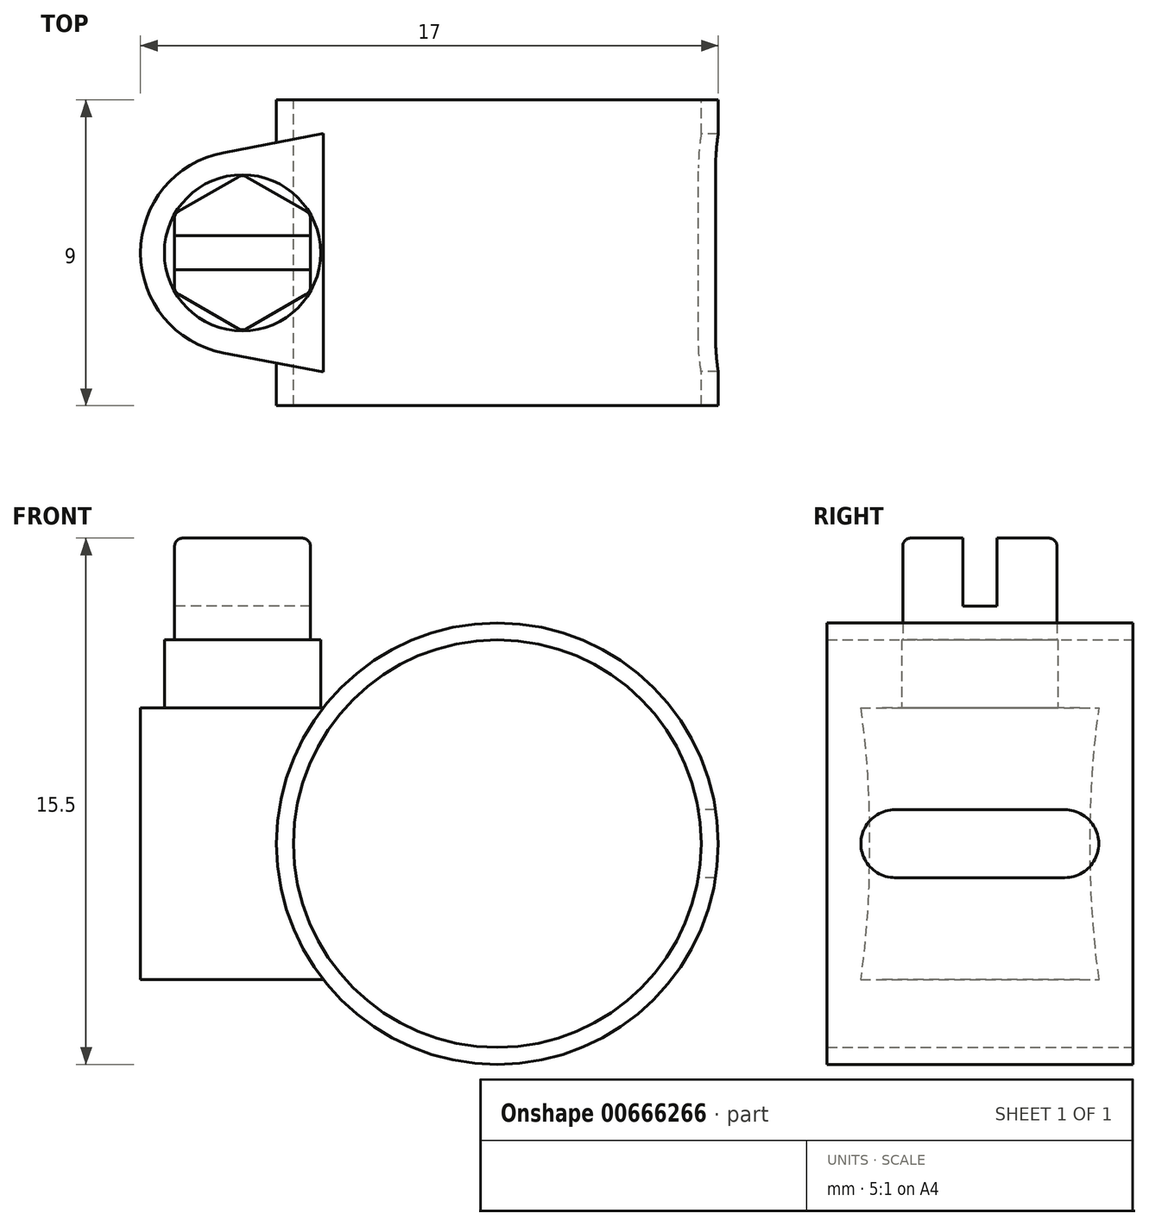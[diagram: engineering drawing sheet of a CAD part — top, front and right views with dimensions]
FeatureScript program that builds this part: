
annotation { "Feature Type Name" : "Feature", "Feature Type Description" : "" }
export const myFeature = defineFeature(function(context is Context, id is Id, definition is map)
    precondition{}
    {
        {
            var Q0;
            Q0=qCreatedBy(makeId("Front.planeOp"),FACE);
            var sketch = newSketch(context, id + "F0", { "sketchPlane" : qUnion([Q0])});
            skCircle(sketch, "E0", {"center": v(0, 0) * mm, "radius": 6.5 * mm});
            skCircle(sketch, "E1", {"center": v(0, 0) * mm, "radius": 6 * mm, "construction": true});
            skSolve(sketch);
        }
        {
            var Q0;
            Q0=qSketchRegion(id+"F0",true);
            extrude(context, id + "F1", {"entities" : qUnion([Q0]), "depth" : 9 * mm, "offsetDistance" : 25 * mm, "symmetric" : true});
        }
        {
            var Q0;
            Q0=qCreatedBy(makeId("Top.planeOp"),FACE);
            var sketch = newSketch(context, id + "F2", { "sketchPlane" : qUnion([Q0])});
            skArc(sketch, "E2", {"start": v(-8.07, 2.95) * mm, "mid": v(-10.5, 0) * mm, "end": v(-8.07, -2.95) * mm});
            skLineSegment(sketch, "E3", {"start": v(-8.07, 2.95) * mm, "end": v(0, 4.5) * mm});
            skLineSegment(sketch, "E4", {"start": v(0, 4.5) * mm, "end": v(0, -4.5) * mm});
            skLineSegment(sketch, "E5", {"start": v(0, -4.5) * mm, "end": v(-8.07, -2.95) * mm});
            skSolve(sketch);
        }
        {
            var Q0;
            Q0=qSketchRegion(id+"F2",true);
            extrude(context, id + "F3", {"entities" : qUnion([Q0]), "operationType" : NewBodyOperationType.ADD, "depth" : 8 * mm, "offsetDistance" : 25 * mm, "symmetric" : true});
        }
        {
            var Q0;
            Q0=makeQuery(id+"F3.opExtrude","CAP_FACE",FACE,{"disambiguationData":[OSD([sQuery(id+"F2.wireOp",EDGE,"E2"),sQuery(id+"F2.wireOp",EDGE,"E3"),sQuery(id+"F2.wireOp",EDGE,"E4"),sQuery(id+"F2.wireOp",EDGE,"E5")])],"isStart":false});
            var sketch = newSketch(context, id + "F4", { "sketchPlane" : qUnion([Q0])});
            skCircle(sketch, "E6.cCircle", {"center": v(-7.5, 0) * mm, "radius": 2 * mm, "construction": true});
            skLineSegment(sketch, "E6.0", {"start": v(-9.5, -1.15) * mm, "end": v(-9.5, 1.15) * mm});
            skLineSegment(sketch, "E6.1", {"start": v(-9.5, 1.15) * mm, "end": v(-7.5, 2.3) * mm});
            skLineSegment(sketch, "E6.2", {"start": v(-7.5, 2.3) * mm, "end": v(-5.5, 1.15) * mm});
            skLineSegment(sketch, "E6.3", {"start": v(-5.5, 1.15) * mm, "end": v(-5.5, -1.15) * mm});
            skLineSegment(sketch, "E6.4", {"start": v(-5.5, -1.15) * mm, "end": v(-7.5, -2.3) * mm});
            skLineSegment(sketch, "E6.5", {"start": v(-7.5, -2.3) * mm, "end": v(-9.5, -1.15) * mm});
            skPoint(sketch, "E6.0.midPoint", {"position": v(-9.5, 0) * mm});
            skSolve(sketch);
        }
        {
            var Q0;
            Q0=qSketchRegion(id+"F4",true);
            extrude(context, id + "F5", {"entities" : qUnion([Q0]), "operationType" : NewBodyOperationType.ADD, "depth" : 5 * mm, "offsetDistance" : 25 * mm});
        }
        {
            var Q0;
            Q0=makeQuery(id+"F1.opExtrude","CAP_FACE",FACE,{"disambiguationData":[OSD([sQuery(id+"F0.wireOp",EDGE,"E0")])],"isStart":true});
            var sketch = newSketch(context, id + "F6", { "sketchPlane" : qUnion([Q0])});
            skCircle(sketch, "E7", {"center": v(0, 0) * mm, "radius": 6 * mm});
            skSolve(sketch);
        }
        {
            var Q0;
            Q0=qSketchRegion(id+"F6",true);
            extrude(context, id + "F7", {"entities" : qUnion([Q0]), "operationType" : NewBodyOperationType.REMOVE, "endBound" : BoundingType.THROUGH_ALL, "oppositeDirection" : true, "depth" : 25 * mm, "offsetDistance" : 25 * mm});
        }
        {
            var Q0;
            Q0=makeQuery(id+"F5.opExtrude","CAP_FACE",FACE,{"disambiguationData":[OSD([sQuery(id+"F4.wireOp",EDGE,"E6.0"),sQuery(id+"F4.wireOp",EDGE,"E6.1"),sQuery(id+"F4.wireOp",EDGE,"E6.2"),sQuery(id+"F4.wireOp",EDGE,"E6.3"),sQuery(id+"F4.wireOp",EDGE,"E6.4"),sQuery(id+"F4.wireOp",EDGE,"E6.5")])],"isStart":false});
            var sketch = newSketch(context, id + "F8", { "sketchPlane" : qUnion([Q0])});
            skLineSegment(sketch, "E8.bottom", {"start": v(-5.5, 0.5) * mm, "end": v(-9.5, 0.5) * mm});
            skLineSegment(sketch, "E8.top", {"start": v(-5.5, -0.5) * mm, "end": v(-9.5, -0.5) * mm});
            skLineSegment(sketch, "E8.left", {"start": v(-5.5, 0.5) * mm, "end": v(-5.5, -0.5) * mm});
            skLineSegment(sketch, "E8.right", {"start": v(-9.5, 0.5) * mm, "end": v(-9.5, -0.5) * mm});
            skPoint(sketch, "E8.middle", {"position": v(-7.5, 0) * mm});
            skSolve(sketch);
        }
        {
            var Q0;
            Q0 = qSketchRegion(id + "F8", true);
            extrude(context, id + "F9", {"entities" : qUnion([Q0]), "operationType" : NewBodyOperationType.REMOVE, "oppositeDirection" : true, "depth" : 2 * mm, "offsetDistance" : 25 * mm});
        }
        {
            var Q0;
            {var subQ0=sQuery(id+"F4.wireOp",EDGE,"E6.0");var subQ1=sQuery(id+"F4.wireOp",EDGE,"E6.1");Q0=makeQuery(id+"F9.boolean.opBoolean","SPLIT",EDGE,{"disambiguationData":[TD([makeQuery(id+"F5.opExtrude","SWEPT_FACE",FACE,{"disambiguationData":[OSD([subQ1])]})])],"derivedFrom":makeQuery(id+"F5.opExtrude","CAP_EDGE",EDGE,{"disambiguationData":[OSD([subQ0])],"isStart":false})});}
            var Q1;
            Q1=makeQuery(id+"F5.opExtrude","CAP_EDGE",EDGE,{"disambiguationData":[OSD([sQuery(id+"F4.wireOp",EDGE,"E6.1")])],"isStart":false});
            var Q2;
            Q2=makeQuery(id+"F5.opExtrude","CAP_EDGE",EDGE,{"disambiguationData":[OSD([sQuery(id+"F4.wireOp",EDGE,"E6.2")])],"isStart":false});
            var Q3;
            {var subQ0=sQuery(id+"F4.wireOp",EDGE,"E6.3");var subQ1=sQuery(id+"F4.wireOp",EDGE,"E6.2");Q3=makeQuery(id+"F9.boolean.opBoolean","SPLIT",EDGE,{"disambiguationData":[TD([makeQuery(id+"F5.opExtrude","SWEPT_FACE",FACE,{"disambiguationData":[OSD([subQ1])]})])],"derivedFrom":makeQuery(id+"F5.opExtrude","CAP_EDGE",EDGE,{"disambiguationData":[OSD([subQ0])],"isStart":false})});}
            var Q4;
            {var subQ0=sQuery(id+"F4.wireOp",EDGE,"E6.4");var subQ1=sQuery(id+"F4.wireOp",EDGE,"E6.3");Q4=makeQuery(id+"F9.boolean.opBoolean","SPLIT",EDGE,{"disambiguationData":[TD([makeQuery(id+"F5.opExtrude","SWEPT_FACE",FACE,{"disambiguationData":[OSD([subQ0])]})])],"derivedFrom":makeQuery(id+"F5.opExtrude","CAP_EDGE",EDGE,{"disambiguationData":[OSD([subQ1])],"isStart":false})});}
            var Q5;
            Q5=makeQuery(id+"F5.opExtrude","CAP_EDGE",EDGE,{"disambiguationData":[OSD([sQuery(id+"F4.wireOp",EDGE,"E6.4")])],"isStart":false});
            var Q6;
            Q6=makeQuery(id+"F5.opExtrude","CAP_EDGE",EDGE,{"disambiguationData":[OSD([sQuery(id+"F4.wireOp",EDGE,"E6.5")])],"isStart":false});
            var Q7;
            {var subQ0=sQuery(id+"F4.wireOp",EDGE,"E6.0");var subQ1=sQuery(id+"F4.wireOp",EDGE,"E6.5");Q7=makeQuery(id+"F9.boolean.opBoolean","SPLIT",EDGE,{"disambiguationData":[TD([makeQuery(id+"F5.opExtrude","SWEPT_FACE",FACE,{"disambiguationData":[OSD([subQ1])]})])],"derivedFrom":makeQuery(id+"F5.opExtrude","CAP_EDGE",EDGE,{"disambiguationData":[OSD([subQ0])],"isStart":false})});}
            var Q8;
            Q8=makeQuery(id+"F5.opExtrude","SWEPT_EDGE",EDGE,{"disambiguationData":[OSD([sQuery(id+"F4.wireOp",EDGE,"E6.0"),sQuery(id+"F4.wireOp",EDGE,"E6.5")])]});
            var Q9;
            Q9=makeQuery(id+"F5.opExtrude","SWEPT_EDGE",EDGE,{"disambiguationData":[OSD([sQuery(id+"F4.wireOp",EDGE,"E6.0"),sQuery(id+"F4.wireOp",EDGE,"E6.1")])]});
            var Q10;
            Q10=makeQuery(id+"F5.opExtrude","SWEPT_EDGE",EDGE,{"disambiguationData":[OSD([sQuery(id+"F4.wireOp",EDGE,"E6.1"),sQuery(id+"F4.wireOp",EDGE,"E6.2")])]});
            var Q11;
            Q11=makeQuery(id+"F5.opExtrude","SWEPT_EDGE",EDGE,{"disambiguationData":[OSD([sQuery(id+"F4.wireOp",EDGE,"E6.2"),sQuery(id+"F4.wireOp",EDGE,"E6.3")])]});
            var Q12;
            Q12=makeQuery(id+"F5.opExtrude","SWEPT_EDGE",EDGE,{"disambiguationData":[OSD([sQuery(id+"F4.wireOp",EDGE,"E6.3"),sQuery(id+"F4.wireOp",EDGE,"E6.4")])]});
            var Q13;
            Q13=makeQuery(id+"F5.opExtrude","SWEPT_EDGE",EDGE,{"disambiguationData":[OSD([sQuery(id+"F4.wireOp",EDGE,"E6.4"),sQuery(id+"F4.wireOp",EDGE,"E6.5")])]});
            fillet(context, id + "F10", {"entities" : qUnion([Q0, Q1, Q2, Q3, Q4, Q5, Q6, Q7, Q8, Q9, Q10, Q11, Q12, Q13]), "radius" : 0.25 * mm, "tangentPropagation" : true, "allowEdgeOverflow" : false});
        }
        {
            var Q0;
            Q0=makeQuery(id+"F3.opExtrude","CAP_FACE",FACE,{"disambiguationData":[OSD([sQuery(id+"F2.wireOp",EDGE,"E2"),sQuery(id+"F2.wireOp",EDGE,"E3"),sQuery(id+"F2.wireOp",EDGE,"E4"),sQuery(id+"F2.wireOp",EDGE,"E5")])],"isStart":false});
            var sketch = newSketch(context, id + "F11", { "sketchPlane" : qUnion([Q0])});
            skCircle(sketch, "E9", {"center": v(-7.5, 0) * mm, "radius": 2.3 * mm});
            skSolve(sketch);
        }
        {
            var Q0;
            Q0 = qSketchRegion(id + "F11", true);
            extrude(context, id + "F12", {"entities" : qUnion([Q0]), "operationType" : NewBodyOperationType.ADD, "depth" : 2 * mm, "offsetDistance" : 25 * mm});
        }
        {
            var Q0;
            Q0=qCreatedBy(makeId("Right.planeOp"),FACE);
            var sketch = newSketch(context, id + "F13", { "sketchPlane" : qUnion([Q0])});
            skLineSegment(sketch, "E10.bottom", {"start": v(-3.5, 1) * mm, "end": v(3.5, 1) * mm});
            skLineSegment(sketch, "E10.top", {"start": v(-3.5, -1) * mm, "end": v(3.5, -1) * mm});
            skLineSegment(sketch, "E10.left", {"start": v(-3.5, 1) * mm, "end": v(-3.5, -1) * mm});
            skLineSegment(sketch, "E10.right", {"start": v(3.5, 1) * mm, "end": v(3.5, -1) * mm});
            skPoint(sketch, "E10.middle", {"position": v(0, 0) * mm});
            skSolve(sketch);
        }
        {
            var Q0;
            Q0 = qSketchRegion(id + "F13", true);
            var Q1;
            Q1=makeQuery(id+"F1.opExtrude","SWEPT_FACE",FACE,{"disambiguationData":[OSD([sQuery(id+"F0.wireOp",EDGE,"E0")])]});
            extrude(context, id + "F14", {"entities" : qUnion([Q0]), "operationType" : NewBodyOperationType.REMOVE, "endBound" : BoundingType.UP_TO_SURFACE, "depth" : 25 * mm, "endBoundEntityFace" : qUnion([Q1]), "offsetDistance" : 25 * mm});
        }
        {
            var Q0;
            Q0=makeQuery(id+"F14.boolean.opBoolean","COPY",EDGE,{"derivedFrom":makeQuery(id+"F14.opExtrude","SWEPT_EDGE",EDGE,{"disambiguationData":[OSD([sQuery(id+"F13.wireOp",EDGE,"E10.top"),sQuery(id+"F13.wireOp",EDGE,"E10.right")])]})});
            var Q1;
            Q1=makeQuery(id+"F14.boolean.opBoolean","COPY",EDGE,{"derivedFrom":makeQuery(id+"F14.opExtrude","SWEPT_EDGE",EDGE,{"disambiguationData":[OSD([sQuery(id+"F13.wireOp",EDGE,"E10.bottom"),sQuery(id+"F13.wireOp",EDGE,"E10.right")])]})});
            var Q2;
            Q2=makeQuery(id+"F14.boolean.opBoolean","COPY",EDGE,{"derivedFrom":makeQuery(id+"F14.opExtrude","SWEPT_EDGE",EDGE,{"disambiguationData":[OSD([sQuery(id+"F13.wireOp",EDGE,"E10.bottom"),sQuery(id+"F13.wireOp",EDGE,"E10.left")])]})});
            var Q3;
            Q3=makeQuery(id+"F14.boolean.opBoolean","COPY",EDGE,{"derivedFrom":makeQuery(id+"F14.opExtrude","SWEPT_EDGE",EDGE,{"disambiguationData":[OSD([sQuery(id+"F13.wireOp",EDGE,"E10.top"),sQuery(id+"F13.wireOp",EDGE,"E10.left")])]})});
            fillet(context, id + "F15", {"entities" : qUnion([Q0, Q1, Q2, Q3]), "radius" : 1 * mm, "tangentPropagation" : true, "allowEdgeOverflow" : false});
        }
    });
